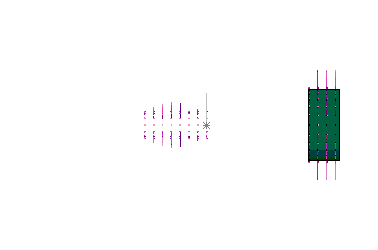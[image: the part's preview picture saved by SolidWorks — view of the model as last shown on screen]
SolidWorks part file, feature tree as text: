
SOLIDWORKS PART (.sldprt)
format: sldprt  version: not decoded by parser v0  size: 1,101,824 bytes
history: native  units: mm
features: sketch x5, plane x3, extrude x2, revolve x2, pattern_linear x2, pattern_circular x2, cut_revolve x1 + 1 further entry (+6 scaffold rows collapsed)
feature tree (24):
  scaffold x6  (default folders/planes/origin — collapsed)
  "Corps de surface"
  plane  "Face"
  plane  "Dessus"
  plane  "Droite"
  sketch  "Esquisse1"  dims[D1=25.0mm]
  extrude  "Lien"  Depth=90mm
  sketch  "Esquisse2"  dims[c1.D1=~1.581401mm c2.D1=20.0deg c2.D2=15.0mm c2.D3=3.0mm c2.D4=0.4mm c2.D5=12.4mm]
  revolve  "Révolution1"  Angle=360deg
  pattern_linear  "Répétition linéaire1"  Count1=8 Count2=1 Spacing1=10mm Spacing2=50mm
  pattern_circular  "Répétition circulaire1"  Count=12 Angle=30deg
  sketch  "Esquisse4"  dims[D1=80.0mm]
  extrude  "Lien2"  Depth=35mm
  sketch  "Esquisse5"  dims[c1.D1=20.0mm c1.D2=39.8mm c1.D3=~4.97906mm c2.D3=20.0deg c2.D4=0.4mm c2.D5=3.0mm c2.D6=34.0mm]
  revolve  "Révolution2"  Angle=360deg
  pattern_linear  "Répétition linéaire2"  Count1=4 Count2=1 Spacing1=10mm Spacing2=50mm
  pattern_circular  "Répétition circulaire2"  Count=24 Angle=15deg
  sketch  "Esquisse3"
  cut_revolve  "Enlèvement de matière-Révolution1"  Angle=360deg
decode coverage: 13 of 14 modeling features carry decoded parameters; 1 rows unclassified (native names shown)
note: ~ marks probable driven/reference dimensions
note: suppression state not decoded; provenance and decode notes live in map.json
